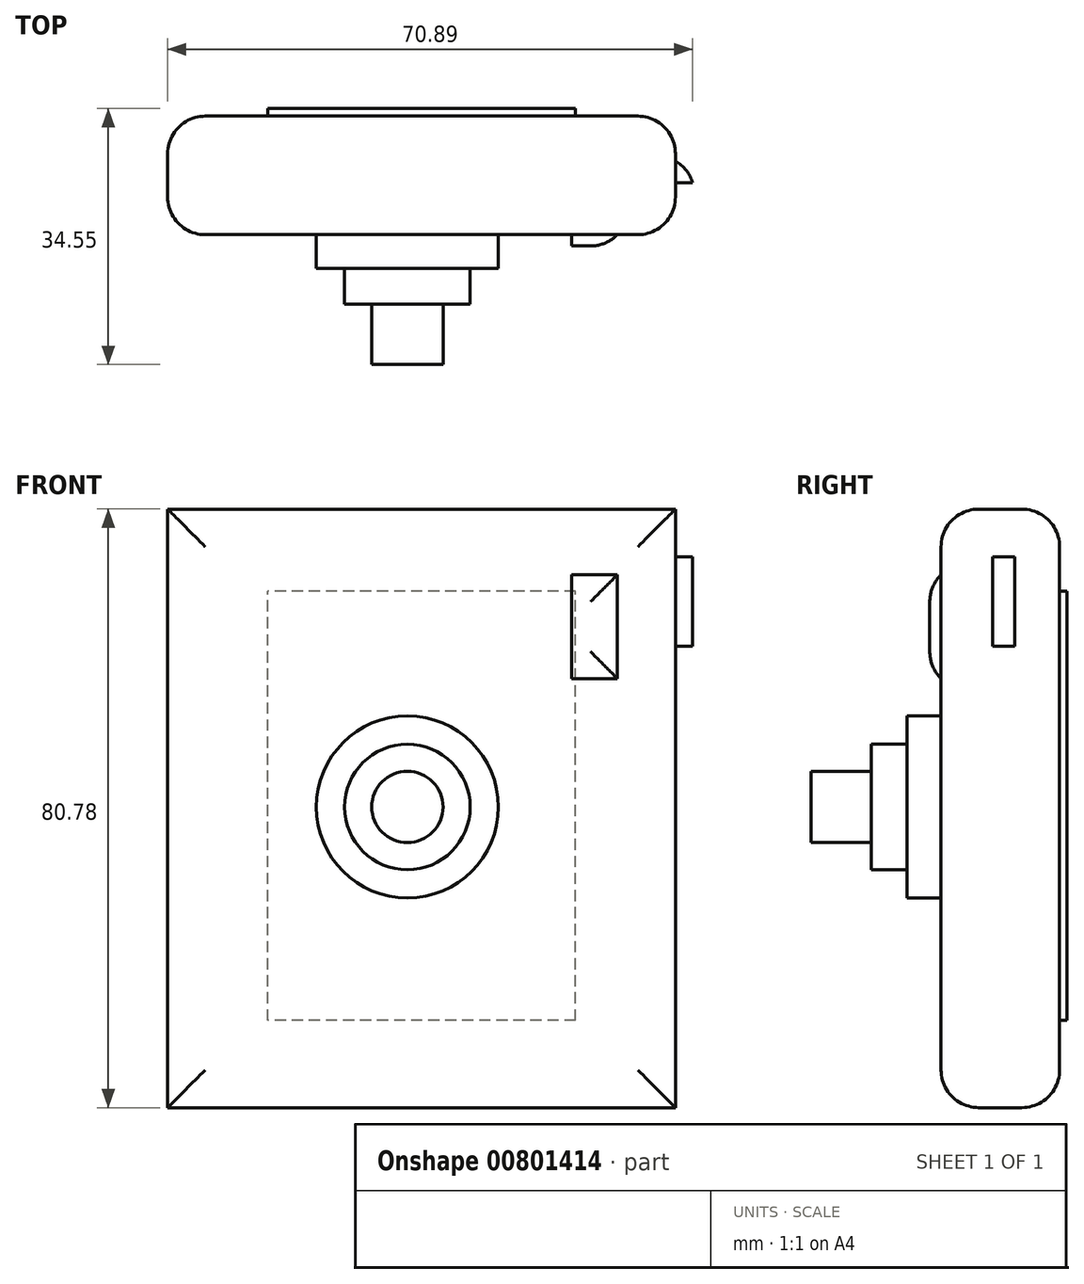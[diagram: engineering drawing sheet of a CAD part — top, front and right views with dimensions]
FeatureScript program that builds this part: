
annotation { "Feature Type Name" : "Feature", "Feature Type Description" : "" }
export const myFeature = defineFeature(function(context is Context, id is Id, definition is map)
    precondition{}
    {
        {
            var Q0;
            Q0=qCreatedBy(makeId("Front.planeOp"),FACE);
            var sketch = newSketch(context, id + "F0", { "sketchPlane" : qUnion([Q0])});
            skLineSegment(sketch, "E0.bottom", {"start": v(-32.37, 40.2) * mm, "end": v(36.19, 40.2) * mm});
            skLineSegment(sketch, "E0.top", {"start": v(-32.37, -40.58) * mm, "end": v(36.19, -40.58) * mm});
            skLineSegment(sketch, "E0.left", {"start": v(-32.37, 40.2) * mm, "end": v(-32.37, -40.58) * mm});
            skLineSegment(sketch, "E0.right", {"start": v(36.19, 40.2) * mm, "end": v(36.19, -40.58) * mm});
            skSolve(sketch);
        }
        {
            var Q0;
            Q0 = qSketchRegion(id + "F0", true);
            extrude(context, id + "F1", {"entities" : qUnion([Q0]), "depth" : 16 * mm, "offsetDistance" : 25.4 * mm});
        }
        {
            var Q0;
            Q0=makeQuery(id+"F1.opExtrude","CAP_FACE",FACE,{"disambiguationData":[OSD([sQuery(id+"F0.wireOp",EDGE,"E0.bottom"),sQuery(id+"F0.wireOp",EDGE,"E0.top"),sQuery(id+"F0.wireOp",EDGE,"E0.left"),sQuery(id+"F0.wireOp",EDGE,"E0.right")])],"isStart":false});
            var sketch = newSketch(context, id + "F2", { "sketchPlane" : qUnion([Q0])});
            skCircle(sketch, "E1", {"center": v(0, 0) * mm, "radius": 12.28 * mm});
            skLineSegment(sketch, "E2.bottom", {"start": v(22.17, 31.33) * mm, "end": v(28.35, 31.33) * mm});
            skLineSegment(sketch, "E2.top", {"start": v(22.17, 17.33) * mm, "end": v(28.35, 17.33) * mm});
            skLineSegment(sketch, "E2.left", {"start": v(22.17, 31.33) * mm, "end": v(22.17, 17.33) * mm});
            skLineSegment(sketch, "E2.right", {"start": v(28.35, 31.33) * mm, "end": v(28.35, 17.33) * mm});
            skSolve(sketch);
        }
        {
            var Q0;
            Q0=makeQuery(id+"F1.opExtrude","SWEPT_FACE",FACE,{"disambiguationData":[OSD([sQuery(id+"F0.wireOp",EDGE,"E0.right")])]});
            var sketch = newSketch(context, id + "F3", { "sketchPlane" : qUnion([Q0])});
            skLineSegment(sketch, "E3.bottom", {"start": v(-6.06, 33.74) * mm, "end": v(-9.01, 33.74) * mm});
            skLineSegment(sketch, "E3.top", {"start": v(-6.06, 21.66) * mm, "end": v(-9.01, 21.66) * mm});
            skLineSegment(sketch, "E3.left", {"start": v(-6.06, 33.74) * mm, "end": v(-6.06, 21.66) * mm});
            skLineSegment(sketch, "E3.right", {"start": v(-9.01, 33.74) * mm, "end": v(-9.01, 21.66) * mm});
            skSolve(sketch);
        }
        {
            var Q0;
            Q0=makeQuery(id+"F2.imprint","IMPRINT",FACE,{"disambiguationData":[TD([[makeQuery(id+"F2.imprint","IMPRINT",EDGE,{"derivedFrom":sQuery(id+"F2.wireOp",EDGE,"E1")}),1.0]])]});
            var Q1;
            Q1=makeQuery(id+"F2.imprint","IMPRINT",FACE,{"disambiguationData":[TD([[makeQuery(id+"F2.imprint","IMPRINT",EDGE,{"derivedFrom":sQuery(id+"F2.wireOp",EDGE,"E2.bottom")}),-1.0]])]});
            extrude(context, id + "F4", {"entities" : qUnion([Q0, Q1]), "operationType" : NewBodyOperationType.ADD, "depth" : 1.52 * mm, "offsetDistance" : 25.4 * mm});
        }
        {
            var Q0;
            Q0=makeQuery(id+"F4.opExtrude","CAP_FACE",FACE,{"disambiguationData":[OSD([sQuery(id+"F2.wireOp",EDGE,"E1")])],"isStart":false});
            extrude(context, id + "F5", {"entities" : qUnion([Q0]), "operationType" : NewBodyOperationType.ADD, "depth" : 3.05 * mm, "offsetDistance" : 25.4 * mm});
        }
        {
            var Q0;
            Q0=makeQuery(id+"F3.imprint","IMPRINT",FACE,{"disambiguationData":[TD([[makeQuery(id+"F3.imprint","IMPRINT",EDGE,{"derivedFrom":sQuery(id+"F3.wireOp",EDGE,"E3.bottom")}),1.0]])]});
            extrude(context, id + "F6", {"entities" : qUnion([Q0]), "operationType" : NewBodyOperationType.ADD, "depth" : 2.54 * mm, "offsetDistance" : 25.4 * mm});
        }
        {
            var Q0;
            Q0=makeQuery(id+"F6.opExtrude","CAP_EDGE",EDGE,{"disambiguationData":[OSD([sQuery(id+"F3.wireOp",EDGE,"E3.left")])],"isStart":false});
            fillet(context, id + "F7", {"entities" : qUnion([Q0]), "radius" : 5.08 * mm, "tangentPropagation" : true, "allowEdgeOverflow" : false});
        }
        {
            var Q0;
            Q0=makeQuery(id+"F5.opExtrude","CAP_FACE",FACE,{"disambiguationData":[OSD([sQuery(id+"F2.wireOp",EDGE,"E1")])],"isStart":false});
            var sketch = newSketch(context, id + "F8", { "sketchPlane" : qUnion([Q0])});
            skCircle(sketch, "E4", {"center": v(0, 0) * mm, "radius": 8.48 * mm});
            skSolve(sketch);
        }
        {
            var Q0;
            Q0=makeQuery(id+"F8.imprint","IMPRINT",FACE,{"disambiguationData":[TD([[makeQuery(id+"F8.imprint","IMPRINT",EDGE,{"derivedFrom":sQuery(id+"F8.wireOp",EDGE,"E4")}),1.0]])]});
            extrude(context, id + "F9", {"entities" : qUnion([Q0]), "operationType" : NewBodyOperationType.ADD, "depth" : 4.83 * mm, "offsetDistance" : 25.4 * mm});
        }
        {
            var Q0;
            Q0=makeQuery(id+"F9.opExtrude","CAP_FACE",FACE,{"disambiguationData":[OSD([sQuery(id+"F8.wireOp",EDGE,"E4")])],"isStart":false});
            var sketch = newSketch(context, id + "F10", { "sketchPlane" : qUnion([Q0])});
            skCircle(sketch, "E5", {"center": v(0, 0) * mm, "radius": 4.81 * mm});
            skSolve(sketch);
        }
        {
            var Q0;
            Q0=makeQuery(id+"F10.imprint","IMPRINT",FACE,{"disambiguationData":[TD([[makeQuery(id+"F10.imprint","IMPRINT",EDGE,{"derivedFrom":sQuery(id+"F10.wireOp",EDGE,"E5")}),1.0]])]});
            extrude(context, id + "F11", {"entities" : qUnion([Q0]), "operationType" : NewBodyOperationType.ADD, "depth" : 8.13 * mm, "offsetDistance" : 25.4 * mm});
        }
        {
            var Q0;
            Q0=makeQuery(id+"F1.opExtrude","CAP_EDGE",EDGE,{"disambiguationData":[OSD([sQuery(id+"F0.wireOp",EDGE,"E0.right")])],"isStart":false});
            var Q1;
            Q1=makeQuery(id+"F1.opExtrude","CAP_EDGE",EDGE,{"disambiguationData":[OSD([sQuery(id+"F0.wireOp",EDGE,"E0.bottom")])],"isStart":false});
            var Q2;
            Q2=makeQuery(id+"F1.opExtrude","CAP_EDGE",EDGE,{"disambiguationData":[OSD([sQuery(id+"F0.wireOp",EDGE,"E0.top")])],"isStart":false});
            var Q3;
            Q3=makeQuery(id+"F1.opExtrude","CAP_EDGE",EDGE,{"disambiguationData":[OSD([sQuery(id+"F0.wireOp",EDGE,"E0.left")])],"isStart":false});
            var Q4;
            Q4=makeQuery(id+"F1.opExtrude","CAP_EDGE",EDGE,{"disambiguationData":[OSD([sQuery(id+"F0.wireOp",EDGE,"E0.top")])],"isStart":true});
            var Q5;
            Q5=makeQuery(id+"F1.opExtrude","CAP_EDGE",EDGE,{"disambiguationData":[OSD([sQuery(id+"F0.wireOp",EDGE,"E0.right")])],"isStart":true});
            var Q6;
            Q6=makeQuery(id+"F1.opExtrude","CAP_EDGE",EDGE,{"disambiguationData":[OSD([sQuery(id+"F0.wireOp",EDGE,"E0.bottom")])],"isStart":true});
            var Q7;
            Q7=makeQuery(id+"F1.opExtrude","CAP_EDGE",EDGE,{"disambiguationData":[OSD([sQuery(id+"F0.wireOp",EDGE,"E0.left")])],"isStart":true});
            fillet(context, id + "F12", {"entities" : qUnion([Q0, Q1, Q2, Q3, Q4, Q5, Q6, Q7]), "radius" : 5.08 * mm, "tangentPropagation" : true, "allowEdgeOverflow" : false});
        }
        {
            var Q0;
            Q0=makeQuery(id+"F4.opExtrude","CAP_EDGE",EDGE,{"disambiguationData":[OSD([sQuery(id+"F2.wireOp",EDGE,"E2.right")])],"isStart":false});
            var Q1;
            Q1=makeQuery(id+"F4.opExtrude","CAP_EDGE",EDGE,{"disambiguationData":[OSD([sQuery(id+"F2.wireOp",EDGE,"E2.bottom")])],"isStart":false});
            var Q2;
            Q2=makeQuery(id+"F4.opExtrude","CAP_EDGE",EDGE,{"disambiguationData":[OSD([sQuery(id+"F2.wireOp",EDGE,"E2.top")])],"isStart":false});
            fillet(context, id + "F13", {"entities" : qUnion([Q0, Q1, Q2]), "radius" : 5.08 * mm, "tangentPropagation" : true, "allowEdgeOverflow" : false});
        }
        {
            var Q0;
            Q0=makeQuery(id+"F1.opExtrude","CAP_FACE",FACE,{"disambiguationData":[OSD([sQuery(id+"F0.wireOp",EDGE,"E0.bottom"),sQuery(id+"F0.wireOp",EDGE,"E0.top"),sQuery(id+"F0.wireOp",EDGE,"E0.left"),sQuery(id+"F0.wireOp",EDGE,"E0.right")])],"isStart":true});
            var sketch = newSketch(context, id + "F14", { "sketchPlane" : qUnion([Q0])});
            skLineSegment(sketch, "E6.bottom", {"start": v(-22.7, -28.8) * mm, "end": v(18.87, -28.8) * mm});
            skLineSegment(sketch, "E6.top", {"start": v(-22.7, 29.14) * mm, "end": v(18.87, 29.14) * mm});
            skLineSegment(sketch, "E6.left", {"start": v(-22.7, -28.8) * mm, "end": v(-22.7, 29.14) * mm});
            skLineSegment(sketch, "E6.right", {"start": v(18.87, -28.8) * mm, "end": v(18.87, 29.14) * mm});
            skSolve(sketch);
        }
        {
            var Q0;
            Q0=makeQuery(id+"F14.imprint","IMPRINT",FACE,{"disambiguationData":[TD([[makeQuery(id+"F14.imprint","IMPRINT",EDGE,{"derivedFrom":sQuery(id+"F14.wireOp",EDGE,"E6.bottom")}),1.0]])]});
            extrude(context, id + "F15", {"entities" : qUnion([Q0]), "operationType" : NewBodyOperationType.ADD, "depth" : 1.02 * mm, "offsetDistance" : 25.4 * mm});
        }
    });
